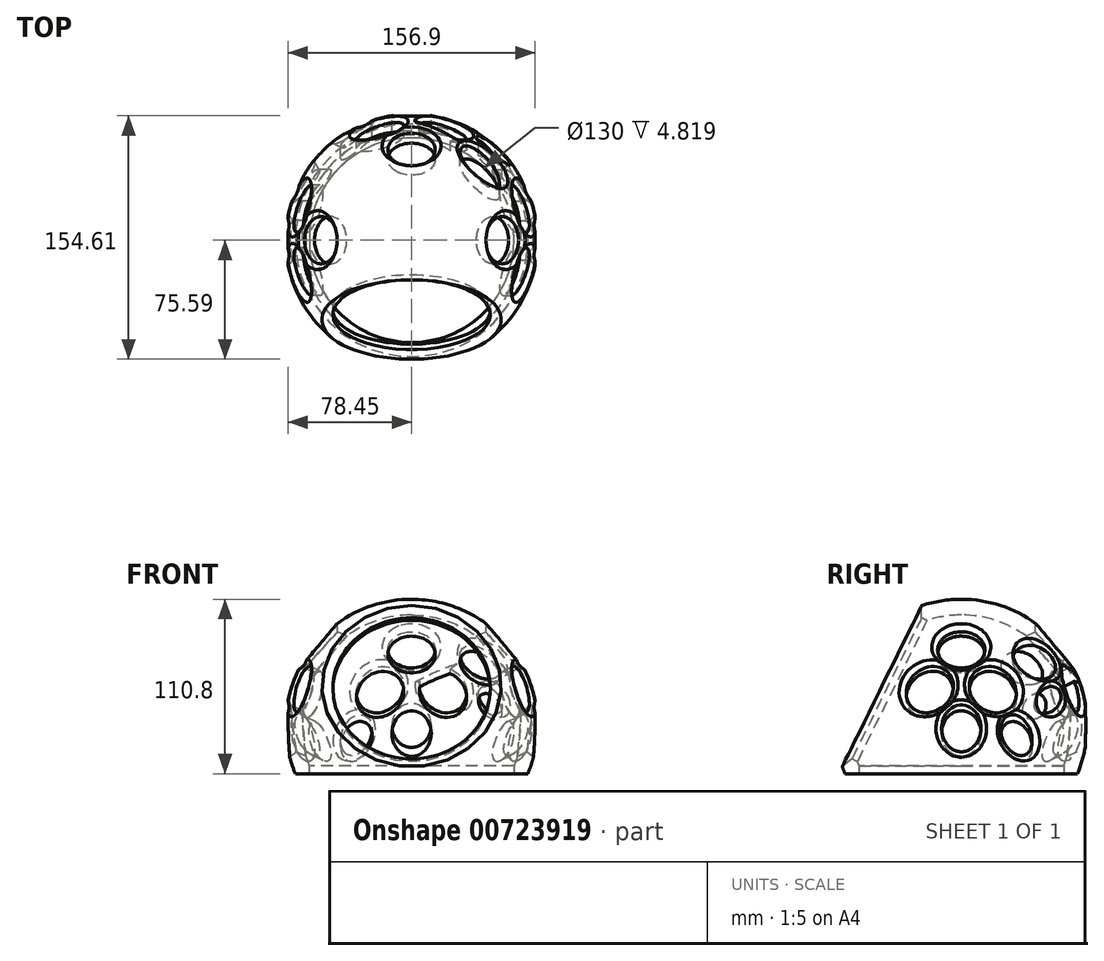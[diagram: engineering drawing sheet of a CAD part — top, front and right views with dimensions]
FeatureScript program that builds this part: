
annotation { "Feature Type Name" : "Feature", "Feature Type Description" : "" }
export const myFeature = defineFeature(function(context is Context, id is Id, definition is map)
    precondition{}
    {
        {
            var Q0;
            Q0=qCreatedBy(makeId("Front.planeOp"),FACE);
            var sketch = newSketch(context, id + "F0", { "sketchPlane" : qUnion([Q0])});
            skCircle(sketch, "E0", {"center": v(0, 0) * mm, "radius": 80 * mm});
            skLineSegment(sketch, "E1", {"start": v(0, 0) * mm, "end": v(0, 80) * mm});
            skLineSegment(sketch, "E2", {"start": v(0, 0) * mm, "end": v(0, -80) * mm});
            skCircle(sketch, "E3", {"center": v(0, 0) * mm, "radius": 70 * mm});
            skCircle(sketch, "E4", {"center": v(0, 0) * mm, "radius": 50 * mm});
            skSolve(sketch);
        }
        {
            var Q0;
            {var subQ0=sQuery(id+"F0.wireOp",EDGE,"E1");var subQ1=sQuery(id+"F0.wireOp",EDGE,"E0");var subQ2=makeQuery(id+"F0.imprint","INTERSECT",VERTEX,{"derivedFrom":[subQ1,subQ0]});Q0=makeQuery(id+"F0.imprint","IMPRINT",FACE,{"disambiguationData":[TD([[makeQuery(id+"F0.imprint","IMPRINT",EDGE,{"disambiguationData":[TD([[subQ2,-1.0]])],"derivedFrom":subQ1}),1.0]])]});}
            var Q1;
            Q1=sQuery(id+"F0.wireOp",EDGE,"E1");
            revolve(context, id + "F1", {"surfaceOperationType" : NewSurfaceOperationType.NEW, "entities" : qUnion([Q0]), "axis" : qUnion([Q1]), "revolveType" : RevolveType.FULL});
        }
        {
            var Q0;
            Q0=qCreatedBy(makeId("Right.planeOp"),FACE);
            var sketch = newSketch(context, id + "F2", { "sketchPlane" : qUnion([Q0])});
            skLineSegment(sketch, "E5", {"start": v(0, 0) * mm, "end": v(-85.81, 28.68) * mm});
            skLineSegment(sketch, "E6", {"start": v(-85.81, 28.68) * mm, "end": v(-77.5, 45.52) * mm});
            skLineSegment(sketch, "E7", {"start": v(0, 0) * mm, "end": v(0, 34.86) * mm});
            skLineSegment(sketch, "E8.MirrorCS", {"start": v(0, 0) * mm, "end": v(85.81, 28.68) * mm});
            skLineSegment(sketch, "E9.MirrorCS", {"start": v(85.81, 28.68) * mm, "end": v(77.5, 45.52) * mm});
            skSolve(sketch);
        }
        {
            var Q0;
            Q0=sQuery(id+"F2.wireOp",EDGE,"E6");
            cPlane(context, id + "F3", {"entities" : qUnion([Q0]), "cplaneType" : CPlaneType.LINE_ANGLE, "offset" : 80 * mm, "angle" : 90 * degree, "width" : 150 * mm, "height" : 150 * mm});
        }
        {
            var Q0;
            Q0=qCreatedBy(id+"F3.planeOp",FACE);
            var sketch = newSketch(context, id + "F4", { "sketchPlane" : qUnion([Q0])});
            skCircle(sketch, "E10", {"center": v(0, 0) * mm, "radius": 50 * mm});
            skSolve(sketch);
        }
        {
            var Q0;
            Q0=makeQuery(id+"F4.imprint","IMPRINT",FACE,{"disambiguationData":[TD([[makeQuery(id+"F4.imprint","IMPRINT",EDGE,{"derivedFrom":sQuery(id+"F4.wireOp",EDGE,"E10")}),1.0]])]});
            extrude(context, id + "F5", {"entities" : qUnion([Q0]), "operationType" : NewBodyOperationType.REMOVE, "depth" : 50 * mm, "offsetDistance" : 25 * mm});
        }
        {
            var Q0;
            Q0=sQuery(id+"F2.wireOp",EDGE,"E9.MirrorCS");
            cPlane(context, id + "F6", {"entities" : qUnion([Q0]), "cplaneType" : CPlaneType.LINE_ANGLE, "offset" : 25 * mm, "angle" : 90 * degree, "width" : 150 * mm, "height" : 150 * mm});
        }
        {
            var Q0;
            Q0=qCreatedBy(id+"F6.planeOp",FACE);
            var sketch = newSketch(context, id + "F7", { "sketchPlane" : qUnion([Q0])});
            skCircle(sketch, "E11", {"center": v(0, 0) * mm, "radius": 50 * mm});
            skSolve(sketch);
        }
        {
            var Q0;
            Q0=qCreatedBy(makeId("Front.planeOp"),FACE);
            var sketch = newSketch(context, id + "F8", { "sketchPlane" : qUnion([Q0])});
            skLineSegment(sketch, "E12", {"start": v(0, -25.2) * mm, "end": v(-90.1, 4.91) * mm});
            skLineSegment(sketch, "E13", {"start": v(-90.1, 4.91) * mm, "end": v(-81.37, 22.6) * mm});
            skLineSegment(sketch, "E14", {"start": v(0, -25.2) * mm, "end": v(0, 11.4) * mm});
            skLineSegment(sketch, "E15.MirrorCS", {"start": v(0, -25.2) * mm, "end": v(90.1, 4.91) * mm});
            skLineSegment(sketch, "E16.MirrorCS", {"start": v(90.1, 4.91) * mm, "end": v(81.37, 22.6) * mm});
            skSolve(sketch);
        }
        {
            var Q0;
            Q0=sQuery(id+"F8.wireOp",EDGE,"E16.MirrorCS");
            cPlane(context, id + "F9", {"entities" : qUnion([Q0]), "cplaneType" : CPlaneType.LINE_ANGLE, "offset" : 25 * mm, "angle" : 0 * degree, "width" : 150 * mm, "height" : 150 * mm});
        }
        {
            var Q0;
            Q0=qCreatedBy(id+"F9.planeOp",FACE);
            var sketch = newSketch(context, id + "F10", { "sketchPlane" : qUnion([Q0])});
            skLineSegment(sketch, "E17", {"start": v(0, 0) * mm, "end": v(0, 17.5) * mm});
            skLineSegment(sketch, "E18", {"start": v(0, 0) * mm, "end": v(0, -10) * mm});
            skCircle(sketch, "E19", {"center": v(0, 17.5) * mm, "radius": 15 * mm});
            skLineSegment(sketch, "E20", {"start": v(0, -10) * mm, "end": v(-20, -10) * mm});
            skLineSegment(sketch, "E21", {"start": v(0, -10) * mm, "end": v(20, -10) * mm});
            skCircle(sketch, "E22", {"center": v(-20, -10) * mm, "radius": 15 * mm});
            skCircle(sketch, "E23", {"center": v(20, -10) * mm, "radius": 15 * mm});
            skLineSegment(sketch, "E24", {"start": v(0, -10) * mm, "end": v(0, -35) * mm});
            skCircle(sketch, "E25", {"center": v(0, -35) * mm, "radius": 12.5 * mm});
            skLineSegment(sketch, "E26", {"start": v(0, -35) * mm, "end": v(35, -35) * mm});
            skCircle(sketch, "E27", {"center": v(35, -35) * mm, "radius": 10 * mm});
            skCircle(sketch, "E28.MirrorC", {"center": v(-35, -35) * mm, "radius": 10 * mm});
            skLineSegment(sketch, "E29.MirrorCS", {"start": v(0, -35) * mm, "end": v(-35, -35) * mm});
            skLineSegment(sketch, "E30", {"start": v(0, -10) * mm, "end": v(0, 0) * mm});
            skLineSegment(sketch, "E31", {"start": v(-5.32, 0) * mm, "end": v(5.82, 0) * mm});
            skSolve(sketch);
        }
        {
            var Q0;
            Q0=makeQuery(id+"F10.imprint","IMPRINT",FACE,{"disambiguationData":[TD([[makeQuery(id+"F10.imprint","IMPRINT",EDGE,{"derivedFrom":sQuery(id+"F10.wireOp",EDGE,"E19")}),1.0]])]});
            var Q1;
            Q1=makeQuery(id+"F10.imprint","IMPRINT",FACE,{"disambiguationData":[TD([[makeQuery(id+"F10.imprint","IMPRINT",EDGE,{"derivedFrom":sQuery(id+"F10.wireOp",EDGE,"E22")}),1.0]])]});
            var Q2;
            Q2=makeQuery(id+"F10.imprint","IMPRINT",FACE,{"disambiguationData":[TD([[makeQuery(id+"F10.imprint","IMPRINT",EDGE,{"derivedFrom":sQuery(id+"F10.wireOp",EDGE,"E23")}),1.0]])]});
            var Q3;
            Q3=makeQuery(id+"F10.imprint","IMPRINT",FACE,{"disambiguationData":[TD([[makeQuery(id+"F10.imprint","IMPRINT",EDGE,{"derivedFrom":sQuery(id+"F10.wireOp",EDGE,"E25")}),1.0]])]});
            var Q4;
            Q4=makeQuery(id+"F10.imprint","IMPRINT",FACE,{"disambiguationData":[TD([[makeQuery(id+"F10.imprint","IMPRINT",EDGE,{"derivedFrom":sQuery(id+"F10.wireOp",EDGE,"E27")}),1.0]])]});
            var Q5;
            Q5=makeQuery(id+"F10.imprint","IMPRINT",FACE,{"disambiguationData":[TD([[makeQuery(id+"F10.imprint","IMPRINT",EDGE,{"derivedFrom":sQuery(id+"F10.wireOp",EDGE,"E28.MirrorC")}),-1.0]])]});
            extrude(context, id + "F11", {"entities" : qUnion([Q0, Q1, Q2, Q3, Q4, Q5]), "operationType" : NewBodyOperationType.REMOVE, "oppositeDirection" : true, "depth" : 50 * mm, "offsetDistance" : 25 * mm});
        }
        {
            var Q0;
            Q0=sQuery(id+"F8.wireOp",EDGE,"E13");
            cPlane(context, id + "F12", {"entities" : qUnion([Q0]), "cplaneType" : CPlaneType.LINE_ANGLE, "offset" : 25 * mm, "angle" : 0 * degree, "width" : 150 * mm, "height" : 150 * mm});
        }
        {
            var Q0;
            Q0=qCreatedBy(id+"F12.planeOp",FACE);
            var sketch = newSketch(context, id + "F13", { "sketchPlane" : qUnion([Q0])});
            skLineSegment(sketch, "E32", {"start": v(0, 0) * mm, "end": v(0, 17.5) * mm});
            skLineSegment(sketch, "E33", {"start": v(0, 0) * mm, "end": v(0, -10) * mm});
            skCircle(sketch, "E34", {"center": v(0, 17.5) * mm, "radius": 15 * mm});
            skLineSegment(sketch, "E35", {"start": v(0, -10) * mm, "end": v(-20, -10) * mm});
            skLineSegment(sketch, "E36", {"start": v(0, -10) * mm, "end": v(20, -10) * mm});
            skCircle(sketch, "E37", {"center": v(-20, -10) * mm, "radius": 15 * mm});
            skCircle(sketch, "E38", {"center": v(20, -10) * mm, "radius": 15 * mm});
            skLineSegment(sketch, "E39", {"start": v(0, -10) * mm, "end": v(0, -35) * mm});
            skCircle(sketch, "E40", {"center": v(0, -35) * mm, "radius": 12.5 * mm});
            skLineSegment(sketch, "E41", {"start": v(0, -35) * mm, "end": v(35, -35) * mm});
            skCircle(sketch, "E42", {"center": v(35, -35) * mm, "radius": 10 * mm});
            skCircle(sketch, "E43.MirrorC", {"center": v(-35, -35) * mm, "radius": 10 * mm});
            skLineSegment(sketch, "E44.MirrorCS", {"start": v(0, -35) * mm, "end": v(-35, -35) * mm});
            skLineSegment(sketch, "E45", {"start": v(0, -10) * mm, "end": v(0, 0) * mm});
            skLineSegment(sketch, "E46", {"start": v(-5.34, 0) * mm, "end": v(5.8, 0) * mm});
            skSolve(sketch);
        }
        {
            var Q0;
            Q0=makeQuery(id+"F13.imprint","IMPRINT",FACE,{"disambiguationData":[TD([[makeQuery(id+"F13.imprint","IMPRINT",EDGE,{"derivedFrom":sQuery(id+"F13.wireOp",EDGE,"E42")}),1.0]])]});
            var Q1;
            {var subQ0=sQuery(id+"F13.wireOp",EDGE,"E41");var subQ1=sQuery(id+"F13.wireOp",EDGE,"E40");var subQ2=makeQuery(id+"F13.imprint","INTERSECT",VERTEX,{"derivedFrom":[subQ1,subQ0]});Q1=makeQuery(id+"F13.imprint","IMPRINT",FACE,{"disambiguationData":[TD([[makeQuery(id+"F13.imprint","IMPRINT",EDGE,{"disambiguationData":[TD([[subQ2,1.0]])],"derivedFrom":subQ1}),1.0]])]});}
            var Q2;
            {var subQ1=sQuery(id+"F13.wireOp",EDGE,"E39");var subQ3=sQuery(id+"F13.wireOp",EDGE,"E40");var subQ4=makeQuery(id+"F13.imprint","INTERSECT",VERTEX,{"derivedFrom":[subQ1,subQ3]});Q2=makeQuery(id+"F13.imprint","IMPRINT",FACE,{"disambiguationData":[TD([[makeQuery(id+"F13.imprint","IMPRINT",EDGE,{"disambiguationData":[TD([[subQ4,-1.0]])],"derivedFrom":subQ3}),1.0]])]});}
            var Q3;
            {var subQ1=sQuery(id+"F13.wireOp",EDGE,"E39");var subQ3=sQuery(id+"F13.wireOp",EDGE,"E40");var subQ4=makeQuery(id+"F13.imprint","INTERSECT",VERTEX,{"derivedFrom":[subQ1,subQ3]});Q3=makeQuery(id+"F13.imprint","IMPRINT",FACE,{"disambiguationData":[TD([[makeQuery(id+"F13.imprint","IMPRINT",EDGE,{"disambiguationData":[TD([[subQ4,1.0]])],"derivedFrom":subQ3}),1.0]])]});}
            var Q4;
            Q4=makeQuery(id+"F13.imprint","IMPRINT",FACE,{"disambiguationData":[TD([[makeQuery(id+"F13.imprint","IMPRINT",EDGE,{"derivedFrom":sQuery(id+"F13.wireOp",EDGE,"E43.MirrorC")}),-1.0]])]});
            var Q5;
            Q5=makeQuery(id+"F13.imprint","IMPRINT",FACE,{"disambiguationData":[TD([[makeQuery(id+"F13.imprint","IMPRINT",EDGE,{"derivedFrom":sQuery(id+"F13.wireOp",EDGE,"E37")}),1.0]])]});
            var Q6;
            Q6=makeQuery(id+"F13.imprint","IMPRINT",FACE,{"disambiguationData":[TD([[makeQuery(id+"F13.imprint","IMPRINT",EDGE,{"derivedFrom":sQuery(id+"F13.wireOp",EDGE,"E38")}),1.0]])]});
            var Q7;
            Q7=makeQuery(id+"F13.imprint","IMPRINT",FACE,{"disambiguationData":[TD([[makeQuery(id+"F13.imprint","IMPRINT",EDGE,{"derivedFrom":sQuery(id+"F13.wireOp",EDGE,"E34")}),1.0]])]});
            extrude(context, id + "F14", {"entities" : qUnion([Q0, Q1, Q2, Q3, Q4, Q5, Q6, Q7]), "operationType" : NewBodyOperationType.REMOVE, "depth" : 50 * mm, "offsetDistance" : 25 * mm});
        }
        {
            var Q0;
            Q0=qCreatedBy(id+"F6.planeOp",FACE);
            var sketch = newSketch(context, id + "F15", { "sketchPlane" : qUnion([Q0])});
            skLineSegment(sketch, "E47", {"start": v(0, 0) * mm, "end": v(0, 17.5) * mm});
            skLineSegment(sketch, "E48", {"start": v(0, 0) * mm, "end": v(0, -10) * mm});
            skCircle(sketch, "E49", {"center": v(0, 17.5) * mm, "radius": 15 * mm});
            skLineSegment(sketch, "E50", {"start": v(0, -10) * mm, "end": v(-20, -10) * mm});
            skLineSegment(sketch, "E51", {"start": v(0, -10) * mm, "end": v(20, -10) * mm});
            skCircle(sketch, "E52", {"center": v(-20, -10) * mm, "radius": 15 * mm});
            skCircle(sketch, "E53", {"center": v(20, -10) * mm, "radius": 15 * mm});
            skLineSegment(sketch, "E54", {"start": v(0, -10) * mm, "end": v(0, -35) * mm});
            skCircle(sketch, "E55", {"center": v(0, -35) * mm, "radius": 12.5 * mm});
            skLineSegment(sketch, "E56", {"start": v(0, -35) * mm, "end": v(35, -35) * mm});
            skCircle(sketch, "E57", {"center": v(35, -35) * mm, "radius": 10 * mm});
            skCircle(sketch, "E58.MirrorC", {"center": v(-35, -35) * mm, "radius": 10 * mm});
            skLineSegment(sketch, "E59.MirrorCS", {"start": v(0, -35) * mm, "end": v(-35, -35) * mm});
            skLineSegment(sketch, "E60", {"start": v(0, -10) * mm, "end": v(0, 0) * mm});
            skLineSegment(sketch, "E61", {"start": v(-5.34, 0) * mm, "end": v(5.8, 0) * mm});
            skLineSegment(sketch, "E62", {"start": v(0, -10) * mm, "end": v(-43.3, 15) * mm});
            skCircle(sketch, "E63", {"center": v(-43.3, 15) * mm, "radius": 12.5 * mm});
            skCircle(sketch, "E64.MirrorC", {"center": v(43.3, 15) * mm, "radius": 12.5 * mm});
            skLineSegment(sketch, "E65", {"start": v(-20, -10) * mm, "end": v(-50, -10) * mm});
            skCircle(sketch, "E66", {"center": v(-50, -10) * mm, "radius": 7.5 * mm});
            skCircle(sketch, "E67.MirrorC", {"center": v(50, -10) * mm, "radius": 7.5 * mm});
            skSolve(sketch);
        }
        {
            var Q0;
            Q0=makeQuery(id+"F15.imprint","IMPRINT",FACE,{"disambiguationData":[TD([[makeQuery(id+"F15.imprint","IMPRINT",EDGE,{"derivedFrom":sQuery(id+"F15.wireOp",EDGE,"E49")}),1.0]])]});
            var Q1;
            Q1=makeQuery(id+"F15.imprint","IMPRINT",FACE,{"disambiguationData":[TD([[makeQuery(id+"F15.imprint","IMPRINT",EDGE,{"derivedFrom":sQuery(id+"F15.wireOp",EDGE,"E52")}),1.0]])]});
            var Q2;
            Q2=makeQuery(id+"F15.imprint","IMPRINT",FACE,{"disambiguationData":[TD([[makeQuery(id+"F15.imprint","IMPRINT",EDGE,{"derivedFrom":sQuery(id+"F15.wireOp",EDGE,"E53")}),1.0]])]});
            var Q3;
            Q3=makeQuery(id+"F15.imprint","IMPRINT",FACE,{"disambiguationData":[TD([[makeQuery(id+"F15.imprint","IMPRINT",EDGE,{"derivedFrom":sQuery(id+"F15.wireOp",EDGE,"E58.MirrorC")}),-1.0]])]});
            var Q4;
            {var subQ0=sQuery(id+"F15.wireOp",EDGE,"E56");var subQ1=sQuery(id+"F15.wireOp",EDGE,"E55");var subQ2=makeQuery(id+"F15.imprint","INTERSECT",VERTEX,{"derivedFrom":[subQ1,subQ0]});Q4=makeQuery(id+"F15.imprint","IMPRINT",FACE,{"disambiguationData":[TD([[makeQuery(id+"F15.imprint","IMPRINT",EDGE,{"disambiguationData":[TD([[subQ2,1.0]])],"derivedFrom":subQ1}),1.0]])]});}
            var Q5;
            Q5=makeQuery(id+"F15.imprint","IMPRINT",FACE,{"disambiguationData":[TD([[makeQuery(id+"F15.imprint","IMPRINT",EDGE,{"derivedFrom":sQuery(id+"F15.wireOp",EDGE,"E57")}),1.0]])]});
            var Q6;
            {var subQ1=sQuery(id+"F15.wireOp",EDGE,"E54");var subQ3=sQuery(id+"F15.wireOp",EDGE,"E55");var subQ4=makeQuery(id+"F15.imprint","INTERSECT",VERTEX,{"derivedFrom":[subQ1,subQ3]});Q6=makeQuery(id+"F15.imprint","IMPRINT",FACE,{"disambiguationData":[TD([[makeQuery(id+"F15.imprint","IMPRINT",EDGE,{"disambiguationData":[TD([[subQ4,-1.0]])],"derivedFrom":subQ3}),1.0]])]});}
            var Q7;
            {var subQ1=sQuery(id+"F15.wireOp",EDGE,"E54");var subQ3=sQuery(id+"F15.wireOp",EDGE,"E55");var subQ4=makeQuery(id+"F15.imprint","INTERSECT",VERTEX,{"derivedFrom":[subQ1,subQ3]});Q7=makeQuery(id+"F15.imprint","IMPRINT",FACE,{"disambiguationData":[TD([[makeQuery(id+"F15.imprint","IMPRINT",EDGE,{"disambiguationData":[TD([[subQ4,1.0]])],"derivedFrom":subQ3}),1.0]])]});}
            var Q8;
            {var subQ0=sQuery(id+"F15.wireOp",EDGE,"E62");var subQ1=sQuery(id+"F15.wireOp",EDGE,"E52");var subQ2=makeQuery(id+"F15.imprint","INTERSECT",VERTEX,{"disambiguationData":[OD(0.0)],"derivedFrom":[subQ1,subQ0]});Q8=makeQuery(id+"F15.imprint","IMPRINT",FACE,{"disambiguationData":[TD([[makeQuery(id+"F15.imprint","IMPRINT",EDGE,{"disambiguationData":[TD([[subQ2,1.0]])],"derivedFrom":subQ1}),1.0]])]});}
            var Q9;
            {var subQ0=sQuery(id+"F15.wireOp",EDGE,"E65");var subQ1=sQuery(id+"F15.wireOp",EDGE,"E50");var subQ2=makeQuery(id+"F15.imprint","INTERSECT",VERTEX,{"derivedFrom":[subQ1,subQ0]});Q9=makeQuery(id+"F15.imprint","IMPRINT",FACE,{"disambiguationData":[TD([[makeQuery(id+"F15.imprint","IMPRINT",EDGE,{"disambiguationData":[TD([[subQ2,1.0]])],"derivedFrom":subQ1}),1.0]])]});}
            var Q10;
            Q10=makeQuery(id+"F15.imprint","IMPRINT",FACE,{"disambiguationData":[TD([[makeQuery(id+"F15.imprint","IMPRINT",EDGE,{"derivedFrom":sQuery(id+"F15.wireOp",EDGE,"E66")}),1.0]])]});
            var Q11;
            Q11=makeQuery(id+"F15.imprint","IMPRINT",FACE,{"disambiguationData":[TD([[makeQuery(id+"F15.imprint","IMPRINT",EDGE,{"derivedFrom":sQuery(id+"F15.wireOp",EDGE,"E63")}),1.0]])]});
            var Q12;
            Q12=makeQuery(id+"F15.imprint","IMPRINT",FACE,{"disambiguationData":[TD([[makeQuery(id+"F15.imprint","IMPRINT",EDGE,{"derivedFrom":sQuery(id+"F15.wireOp",EDGE,"E64.MirrorC")}),-1.0]])]});
            var Q13;
            Q13=makeQuery(id+"F15.imprint","IMPRINT",FACE,{"disambiguationData":[TD([[makeQuery(id+"F15.imprint","IMPRINT",EDGE,{"derivedFrom":sQuery(id+"F15.wireOp",EDGE,"E67.MirrorC")}),-1.0]])]});
            extrude(context, id + "F16", {"entities" : qUnion([Q0, Q1, Q2, Q3, Q4, Q5, Q6, Q7, Q8, Q9, Q10, Q11, Q12, Q13]), "operationType" : NewBodyOperationType.REMOVE, "oppositeDirection" : true, "depth" : 60 * mm, "offsetDistance" : 25 * mm});
        }
        {
            var Q0;
            Q0=qCreatedBy(makeId("Top.planeOp"),FACE);
            var sketch = newSketch(context, id + "F17", { "sketchPlane" : qUnion([Q0])});
            skCircle(sketch, "E68", {"center": v(0, 0) * mm, "radius": 17.5 * mm});
            skLineSegment(sketch, "E69", {"start": v(0, 0) * mm, "end": v(0, 32.5) * mm});
            skCircle(sketch, "E70", {"center": v(0, 32.5) * mm, "radius": 10 * mm});
            skLineSegment(sketch, "E71", {"start": v(0, 0) * mm, "end": v(-32.5, 0) * mm});
            skCircle(sketch, "E72", {"center": v(-32.5, 0) * mm, "radius": 10 * mm});
            skLineSegment(sketch, "E73", {"start": v(0, 0) * mm, "end": v(-29.42, 27.1) * mm});
            skCircle(sketch, "E74", {"center": v(-29.42, 27.1) * mm, "radius": 12.5 * mm});
            skCircle(sketch, "E75.MirrorC", {"center": v(32.5, 0) * mm, "radius": 10 * mm});
            skCircle(sketch, "E76.MirrorC", {"center": v(29.42, 27.1) * mm, "radius": 12.5 * mm});
            skSolve(sketch);
        }
        {
            var Q0;
            Q0=qCreatedBy(makeId("Top.planeOp"),FACE);
            cPlane(context, id + "F18", {"entities" : qUnion([Q0]), "cplaneType" : CPlaneType.OFFSET, "offset" : 80 * mm, "oppositeDirection" : true, "width" : 150 * mm, "height" : 150 * mm});
        }
        {
            var Q0;
            Q0=qCreatedBy(id+"F18.planeOp",FACE);
            var sketch = newSketch(context, id + "F19", { "sketchPlane" : qUnion([Q0])});
            skCircle(sketch, "E77", {"center": v(0, 0) * mm, "radius": 65 * mm});
            skSolve(sketch);
        }
        {
            var Q0;
            Q0=makeQuery(id+"F19.imprint","IMPRINT",FACE,{"disambiguationData":[TD([[makeQuery(id+"F19.imprint","IMPRINT",EDGE,{"derivedFrom":sQuery(id+"F19.wireOp",EDGE,"E77")}),1.0]])]});
            extrude(context, id + "F20", {"entities" : qUnion([Q0]), "operationType" : NewBodyOperationType.REMOVE, "depth" : 80.6 * mm, "offsetDistance" : 25 * mm});
        }
        {
            var Q0;
            Q0=qCreatedBy(id+"F18.planeOp",FACE);
            var sketch = newSketch(context, id + "F21", { "sketchPlane" : qUnion([Q0])});
            skLineSegment(sketch, "E78.bottom", {"start": v(-106.42, -86.88) * mm, "end": v(105.78, -86.88) * mm});
            skLineSegment(sketch, "E78.top", {"start": v(-106.42, 98.95) * mm, "end": v(105.78, 98.95) * mm});
            skLineSegment(sketch, "E78.left", {"start": v(-106.42, -86.88) * mm, "end": v(-106.42, 98.95) * mm});
            skLineSegment(sketch, "E78.right", {"start": v(105.78, -86.88) * mm, "end": v(105.78, 98.95) * mm});
            skSolve(sketch);
        }
        {
            var Q0;
            Q0=makeQuery(id+"F21.imprint","IMPRINT",FACE,{"disambiguationData":[TD([[makeQuery(id+"F21.imprint","IMPRINT",EDGE,{"derivedFrom":sQuery(id+"F21.wireOp",EDGE,"E78.bottom")}),1.0]])]});
            extrude(context, id + "F22", {"entities" : qUnion([Q0]), "operationType" : NewBodyOperationType.REMOVE, "depth" : 49.2 * mm, "offsetDistance" : 25 * mm});
        }
        {
            var Q0;
            Q0=makeQuery(id+"F5.boolean.opBoolean","INTERSECT",EDGE,{"derivedFrom":[makeQuery(id+"F1.opRevolve","SWEPT_FACE",FACE,{"disambiguationData":[OSD([sQuery(id+"F0.wireOp",EDGE,"E0")])]}),makeQuery(id+"F5.opExtrude","SWEPT_FACE",FACE,{"disambiguationData":[OSD([sQuery(id+"F4.wireOp",EDGE,"E10")])]})]});
            var Q1;
            Q1=makeQuery(id+"FtjeLi8Kd9lvvUd_1.boolean.opBoolean","INTERSECT",EDGE,{"derivedFrom":[makeQuery(id+"F1.opRevolve","SWEPT_FACE",FACE,{"disambiguationData":[OSD([sQuery(id+"F0.wireOp",EDGE,"E0")])]}),makeQuery(id+"FtjeLi8Kd9lvvUd_1.opExtrude","SWEPT_FACE",FACE,{"disambiguationData":[OSD([sQuery(id+"F7.wireOp",EDGE,"E11")])]})]});
            chamfer(context, id + "F23", {"entities" : qUnion([Q0, Q1]), "chamferType" : ChamferType.OFFSET_ANGLE, "width" : 9 * mm, "oppositeDirection" : false, "angle" : 60 * degree, "tangentPropagation" : true});
        }
        {
            var Q0;
            Q0=makeQuery(id+"F11.boolean.opBoolean","INTERSECT",EDGE,{"derivedFrom":[makeQuery(id+"F1.opRevolve","SWEPT_FACE",FACE,{"disambiguationData":[OSD([sQuery(id+"F0.wireOp",EDGE,"E0")])]}),makeQuery(id+"F11.opExtrude","SWEPT_FACE",FACE,{"disambiguationData":[OSD([sQuery(id+"F10.wireOp",EDGE,"E22")])]})]});
            var Q1;
            Q1=makeQuery(id+"F11.boolean.opBoolean","INTERSECT",EDGE,{"derivedFrom":[makeQuery(id+"F1.opRevolve","SWEPT_FACE",FACE,{"disambiguationData":[OSD([sQuery(id+"F0.wireOp",EDGE,"E0")])]}),makeQuery(id+"F11.opExtrude","SWEPT_FACE",FACE,{"disambiguationData":[OSD([sQuery(id+"F10.wireOp",EDGE,"E23")])]})]});
            var Q2;
            Q2=makeQuery(id+"F11.boolean.opBoolean","INTERSECT",EDGE,{"derivedFrom":[makeQuery(id+"F1.opRevolve","SWEPT_FACE",FACE,{"disambiguationData":[OSD([sQuery(id+"F0.wireOp",EDGE,"E0")])]}),makeQuery(id+"F11.opExtrude","SWEPT_FACE",FACE,{"disambiguationData":[OSD([sQuery(id+"F10.wireOp",EDGE,"E28.MirrorC")])]})]});
            var Q3;
            Q3=makeQuery(id+"F11.boolean.opBoolean","INTERSECT",EDGE,{"derivedFrom":[makeQuery(id+"F1.opRevolve","SWEPT_FACE",FACE,{"disambiguationData":[OSD([sQuery(id+"F0.wireOp",EDGE,"E0")])]}),makeQuery(id+"F11.opExtrude","SWEPT_FACE",FACE,{"disambiguationData":[OSD([sQuery(id+"F10.wireOp",EDGE,"E25")])]})]});
            var Q4;
            Q4=makeQuery(id+"F11.boolean.opBoolean","INTERSECT",EDGE,{"derivedFrom":[makeQuery(id+"F1.opRevolve","SWEPT_FACE",FACE,{"disambiguationData":[OSD([sQuery(id+"F0.wireOp",EDGE,"E0")])]}),makeQuery(id+"F11.opExtrude","SWEPT_FACE",FACE,{"disambiguationData":[OSD([sQuery(id+"F10.wireOp",EDGE,"E27")])]})]});
            var Q5;
            Q5=makeQuery(id+"F14.boolean.opBoolean","INTERSECT",EDGE,{"derivedFrom":[makeQuery(id+"F1.opRevolve","SWEPT_FACE",FACE,{"disambiguationData":[OSD([sQuery(id+"F0.wireOp",EDGE,"E0")])]}),makeQuery(id+"F14.opExtrude","SWEPT_FACE",FACE,{"disambiguationData":[OSD([sQuery(id+"F13.wireOp",EDGE,"E38")])]})]});
            var Q6;
            Q6=makeQuery(id+"F14.boolean.opBoolean","INTERSECT",EDGE,{"derivedFrom":[makeQuery(id+"F1.opRevolve","SWEPT_FACE",FACE,{"disambiguationData":[OSD([sQuery(id+"F0.wireOp",EDGE,"E0")])]}),makeQuery(id+"F14.opExtrude","SWEPT_FACE",FACE,{"disambiguationData":[OSD([sQuery(id+"F13.wireOp",EDGE,"E37")])]})]});
            var Q7;
            Q7=makeQuery(id+"F14.boolean.opBoolean","INTERSECT",EDGE,{"derivedFrom":[makeQuery(id+"F1.opRevolve","SWEPT_FACE",FACE,{"disambiguationData":[OSD([sQuery(id+"F0.wireOp",EDGE,"E0")])]}),makeQuery(id+"F14.opExtrude","SWEPT_FACE",FACE,{"disambiguationData":[OSD([sQuery(id+"F13.wireOp",EDGE,"E42")])]})]});
            var Q8;
            Q8=makeQuery(id+"F14.boolean.opBoolean","INTERSECT",EDGE,{"derivedFrom":[makeQuery(id+"F1.opRevolve","SWEPT_FACE",FACE,{"disambiguationData":[OSD([sQuery(id+"F0.wireOp",EDGE,"E0")])]}),makeQuery(id+"F14.opExtrude","SWEPT_FACE",FACE,{"disambiguationData":[OSD([sQuery(id+"F13.wireOp",EDGE,"E40")])]})]});
            var Q9;
            Q9=makeQuery(id+"F14.boolean.opBoolean","INTERSECT",EDGE,{"derivedFrom":[makeQuery(id+"F1.opRevolve","SWEPT_FACE",FACE,{"disambiguationData":[OSD([sQuery(id+"F0.wireOp",EDGE,"E0")])]}),makeQuery(id+"F14.opExtrude","SWEPT_FACE",FACE,{"disambiguationData":[OSD([sQuery(id+"F13.wireOp",EDGE,"E43.MirrorC")])]})]});
            var Q10;
            Q10=makeQuery(id+"F16.boolean.opBoolean","INTERSECT",EDGE,{"derivedFrom":[makeQuery(id+"F1.opRevolve","SWEPT_FACE",FACE,{"disambiguationData":[OSD([sQuery(id+"F0.wireOp",EDGE,"E0")])]}),makeQuery(id+"F16.opExtrude","SWEPT_FACE",FACE,{"disambiguationData":[OSD([sQuery(id+"F15.wireOp",EDGE,"E52")])]})]});
            var Q11;
            Q11=makeQuery(id+"F16.boolean.opBoolean","INTERSECT",EDGE,{"derivedFrom":[makeQuery(id+"F1.opRevolve","SWEPT_FACE",FACE,{"disambiguationData":[OSD([sQuery(id+"F0.wireOp",EDGE,"E0")])]}),makeQuery(id+"F16.opExtrude","SWEPT_FACE",FACE,{"disambiguationData":[OSD([sQuery(id+"F15.wireOp",EDGE,"E53")])]})]});
            var Q12;
            Q12=makeQuery(id+"F16.boolean.opBoolean","INTERSECT",EDGE,{"derivedFrom":[makeQuery(id+"F1.opRevolve","SWEPT_FACE",FACE,{"disambiguationData":[OSD([sQuery(id+"F0.wireOp",EDGE,"E0")])]}),makeQuery(id+"F16.opExtrude","SWEPT_FACE",FACE,{"disambiguationData":[OSD([sQuery(id+"F15.wireOp",EDGE,"E58.MirrorC")])]})]});
            var Q13;
            Q13=makeQuery(id+"F16.boolean.opBoolean","INTERSECT",EDGE,{"derivedFrom":[makeQuery(id+"F1.opRevolve","SWEPT_FACE",FACE,{"disambiguationData":[OSD([sQuery(id+"F0.wireOp",EDGE,"E0")])]}),makeQuery(id+"F16.opExtrude","SWEPT_FACE",FACE,{"disambiguationData":[OSD([sQuery(id+"F15.wireOp",EDGE,"E57")])]})]});
            var Q14;
            Q14=makeQuery(id+"F11.boolean.opBoolean","INTERSECT",EDGE,{"derivedFrom":[makeQuery(id+"F1.opRevolve","SWEPT_FACE",FACE,{"disambiguationData":[OSD([sQuery(id+"F0.wireOp",EDGE,"E0")])]}),makeQuery(id+"F11.opExtrude","SWEPT_FACE",FACE,{"disambiguationData":[OSD([sQuery(id+"F10.wireOp",EDGE,"E19")])]})]});
            var Q15;
            Q15=makeQuery(id+"F16.boolean.opBoolean","INTERSECT",EDGE,{"derivedFrom":[makeQuery(id+"F1.opRevolve","SWEPT_FACE",FACE,{"disambiguationData":[OSD([sQuery(id+"F0.wireOp",EDGE,"E0")])]}),makeQuery(id+"F16.opExtrude","SWEPT_FACE",FACE,{"disambiguationData":[OSD([sQuery(id+"F15.wireOp",EDGE,"E49")])]})]});
            var Q16;
            Q16=makeQuery(id+"F14.boolean.opBoolean","INTERSECT",EDGE,{"derivedFrom":[makeQuery(id+"F1.opRevolve","SWEPT_FACE",FACE,{"disambiguationData":[OSD([sQuery(id+"F0.wireOp",EDGE,"E0")])]}),makeQuery(id+"F14.opExtrude","SWEPT_FACE",FACE,{"disambiguationData":[OSD([sQuery(id+"F13.wireOp",EDGE,"E34")])]})]});
            var Q17;
            Q17=makeQuery(id+"F16.boolean.opBoolean","INTERSECT",EDGE,{"derivedFrom":[makeQuery(id+"F1.opRevolve","SWEPT_FACE",FACE,{"disambiguationData":[OSD([sQuery(id+"F0.wireOp",EDGE,"E0")])]}),makeQuery(id+"F16.opExtrude","SWEPT_FACE",FACE,{"disambiguationData":[OSD([sQuery(id+"F15.wireOp",EDGE,"E66")])]})]});
            var Q18;
            Q18=makeQuery(id+"F16.boolean.opBoolean","INTERSECT",EDGE,{"derivedFrom":[makeQuery(id+"F1.opRevolve","SWEPT_FACE",FACE,{"disambiguationData":[OSD([sQuery(id+"F0.wireOp",EDGE,"E0")])]}),makeQuery(id+"F16.opExtrude","SWEPT_FACE",FACE,{"disambiguationData":[OSD([sQuery(id+"F15.wireOp",EDGE,"E63")])]})]});
            var Q19;
            Q19=makeQuery(id+"F16.boolean.opBoolean","INTERSECT",EDGE,{"derivedFrom":[makeQuery(id+"F1.opRevolve","SWEPT_FACE",FACE,{"disambiguationData":[OSD([sQuery(id+"F0.wireOp",EDGE,"E0")])]}),makeQuery(id+"F16.opExtrude","SWEPT_FACE",FACE,{"disambiguationData":[OSD([sQuery(id+"F15.wireOp",EDGE,"E67.MirrorC")])]})]});
            var Q20;
            Q20=makeQuery(id+"F16.boolean.opBoolean","INTERSECT",EDGE,{"derivedFrom":[makeQuery(id+"F1.opRevolve","SWEPT_FACE",FACE,{"disambiguationData":[OSD([sQuery(id+"F0.wireOp",EDGE,"E0")])]}),makeQuery(id+"F16.opExtrude","SWEPT_FACE",FACE,{"disambiguationData":[OSD([sQuery(id+"F15.wireOp",EDGE,"E64.MirrorC")])]})]});
            var Q21;
            Q21=makeQuery(id+"F2Lt7VqEDh4wjAF_1.boolean.opBoolean","INTERSECT",EDGE,{"derivedFrom":[makeQuery(id+"F1.opRevolve","SWEPT_FACE",FACE,{"disambiguationData":[OSD([sQuery(id+"F0.wireOp",EDGE,"E0")])]}),makeQuery(id+"F2Lt7VqEDh4wjAF_1.opExtrude","SWEPT_FACE",FACE,{"disambiguationData":[OSD([sQuery(id+"F17.wireOp",EDGE,"E74")])]})]});
            var Q22;
            Q22=makeQuery(id+"F2Lt7VqEDh4wjAF_1.boolean.opBoolean","INTERSECT",EDGE,{"derivedFrom":[makeQuery(id+"F1.opRevolve","SWEPT_FACE",FACE,{"disambiguationData":[OSD([sQuery(id+"F0.wireOp",EDGE,"E0")])]}),makeQuery(id+"F2Lt7VqEDh4wjAF_1.opExtrude","SWEPT_FACE",FACE,{"disambiguationData":[OSD([sQuery(id+"F17.wireOp",EDGE,"E72")])]})]});
            var Q23;
            Q23=makeQuery(id+"F2Lt7VqEDh4wjAF_1.boolean.opBoolean","INTERSECT",EDGE,{"derivedFrom":[makeQuery(id+"F1.opRevolve","SWEPT_FACE",FACE,{"disambiguationData":[OSD([sQuery(id+"F0.wireOp",EDGE,"E0")])]}),makeQuery(id+"F2Lt7VqEDh4wjAF_1.opExtrude","SWEPT_FACE",FACE,{"disambiguationData":[OSD([sQuery(id+"F17.wireOp",EDGE,"E70")])]})]});
            var Q24;
            Q24=makeQuery(id+"FUWBO79qtwdj0IJ_1.boolean.opBoolean","INTERSECT",EDGE,{"derivedFrom":[makeQuery(id+"F1.opRevolve","SWEPT_FACE",FACE,{"disambiguationData":[OSD([sQuery(id+"F0.wireOp",EDGE,"E0")])]}),makeQuery(id+"FUWBO79qtwdj0IJ_1.opExtrude","SWEPT_FACE",FACE,{"disambiguationData":[OSD([sQuery(id+"F17.wireOp",EDGE,"E68")])]})]});
            var Q25;
            Q25=makeQuery(id+"F2Lt7VqEDh4wjAF_1.boolean.opBoolean","INTERSECT",EDGE,{"derivedFrom":[makeQuery(id+"F1.opRevolve","SWEPT_FACE",FACE,{"disambiguationData":[OSD([sQuery(id+"F0.wireOp",EDGE,"E0")])]}),makeQuery(id+"F2Lt7VqEDh4wjAF_1.opExtrude","SWEPT_FACE",FACE,{"disambiguationData":[OSD([sQuery(id+"F17.wireOp",EDGE,"E76.MirrorC")])]})]});
            var Q26;
            Q26=makeQuery(id+"F2Lt7VqEDh4wjAF_1.boolean.opBoolean","INTERSECT",EDGE,{"derivedFrom":[makeQuery(id+"F1.opRevolve","SWEPT_FACE",FACE,{"disambiguationData":[OSD([sQuery(id+"F0.wireOp",EDGE,"E0")])]}),makeQuery(id+"F2Lt7VqEDh4wjAF_1.opExtrude","SWEPT_FACE",FACE,{"disambiguationData":[OSD([sQuery(id+"F17.wireOp",EDGE,"E75.MirrorC")])]})]});
            chamfer(context, id + "F24", {"entities" : qUnion([Q0, Q1, Q2, Q3, Q4, Q5, Q6, Q7, Q8, Q9, Q10, Q11, Q12, Q13, Q14, Q15, Q16, Q17, Q18, Q19, Q20, Q21, Q22, Q23, Q24, Q25, Q26]), "width" : 3 * mm, "tangentPropagation" : true});
        }
    });
